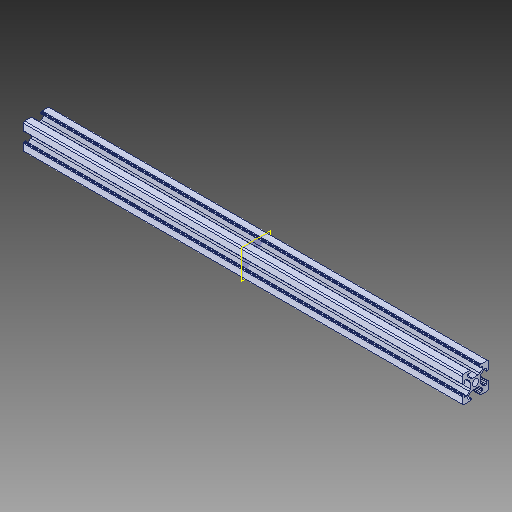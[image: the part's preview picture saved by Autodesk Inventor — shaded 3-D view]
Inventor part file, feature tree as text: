
AUTODESK INVENTOR PART (.ipt)
format: ipt  version: 2018 (Build 220112000, 112)  size: 371,712 bytes
history: native  units: in
note: dims shown in document units (in); Inventor stores cm internally (conversion verified against a paired STEP export)
features: extrude x1, plane x1, sketch x1, projected_geometry x1, fillet x1
ambient origin geometry x8: Origin, YZ Plane, XZ Plane, XY Plane, X Axis, Y Axis, Z Axis, Center Point
bodies: Solid1 (feature_tree)
feature tree (5):
  extrude  "Extrusion2"  [1 undecoded]
  plane  "Work Plane1"
  sketch  "Sketch3"  dims[d2=9.0551in d3=0.0in]
  projected_geometry  "Projected Loop2"
  fillet  "Fillet5"  [1 undecoded]
note: 2 required parameter values undecoded (feature->parameter linkage not recoverable at this tier; creation-order binding heuristic only, values carry confidence <= 0.55)
